# Revit family: RN 82204 Optipress-Aquaplus-Valvola diritta
name_source: partatom
category: Rohrzubehör
units: mm (PartAtom-declared; Revit-internal decimal feet)

## family parameters
Arbeitsebenenbasiert = Nein
Beim Laden mit Abzugskörper schneiden = Nein
Bemaßung runder Anschluss = Durchmesser verwenden
Gemeinsam genutzt = Nein
Immer vertikal = Ja
Teiletyp = Ventil - Zerlegung in

## types (7) — shared parameters
1.010.00.2 Number of the part of the guideline = 17
1.010.00.3 Issue date (month) of the guideline = 201601
1.010.00.4 Manufacturer name = R. Nussbaum AG
1.010.00.5 Revision date of the file = 20190528
1.100.00.3 Sort number for display sequence = 1
1.100.00.4 Product designation = Rubinetti di chiusura
1.960/3L.00.8 Link (URL) = https://www.nussbaum.ch
17.700.00.4 valve assembly type = 1
17.700.00.7 maximum operating temperature TB [°C] = 90
17.700.00.8 maximum operating pressure(working pressure) ps [1.0 · 105 Pa] = 16
Connector Visibility = Nein
EnclosingSpace Visibility = Nein

## per-type parameters (varying)
| type | 1.800.00.3 BS number | 1.810.00.3 Manufacturer’s reference number | 1.810.00.4 DATANORM number | 1.810.00.5 StLB number | 1.810.00.6 GTIN number | 17.700.00.30 product description | 17.700.00.5 nominal size DN | 17.700.00.6 kvs-value [m3/h] | CONNECTOR0_DIAMETER_dX_0r | CONNECTOR0_dX_00 | CONNECTOR0_dX_01 | CONNECTOR0_ref_dX | CONNECTOR1_DIAMETER_dX_0r | CONNECTOR1_dX_00 | CONNECTOR1_dX_01 | CONNECTOR1_ref_dX | R. Nussbaum AG 82204.22 it Visibility | R. Nussbaum AG 82204.23 it Visibility | R. Nussbaum AG 82204.24 it Visibility | R. Nussbaum AG 82204.25 it Visibility | R. Nussbaum AG 82204.26 it Visibility | R. Nussbaum AG 82204.27 it Visibility | R. Nussbaum AG 82204.28 it Visibility |
| DN 12 | 001076???0000000000000000000020070000000000000000100000000 | 82204.22 | 82204.22 | 623.422 | 7612945732965 | 82204.22, Optipress-Aquaplus-Valvola diritta, DN=12 | 12 | 2.93 | 12 mm  [stored 0.0393701 ft] | 45 mm | 23 mm | 23 mm | 12 mm  [stored 0.0393701 ft] | 23 mm | 45 mm | 23 mm | Ja | Nein | Nein | Nein | Nein | Nein | Nein |
| DN 15 | 001076???0000000000000000000020070000000000000000200000000 | 82204.23 | 82204.23 | 623.423 | 7612945732972 | 82204.23, Optipress-Aquaplus-Valvola diritta, DN=15 | 15 | 3.61 | 15 mm | 45 mm | 23 mm | 23 mm | 15 mm | 23 mm | 45 mm | 23 mm | Nein | Ja | Nein | Nein | Nein | Nein | Nein |
| DN 20 | 001076???0000000000000000000020070000000000000000300000000 | 82204.24 | 82204.24 | 623.424 | 7612945732989 | 82204.24, Optipress-Aquaplus-Valvola diritta, DN=20 | 20 | 5.86 | 20 mm | 50 mm | 27 mm | 27 mm | 20 mm | 27 mm | 50 mm | 27 mm | Nein | Nein | Ja | Nein | Nein | Nein | Nein |
| DN 25 | 001076???0000000000000000000020070000000000000000400000000 | 82204.25 | 82204.25 | 623.425 | 7612945728807 | 82204.25, Optipress-Aquaplus-Valvola diritta, DN=25 | 25 | 9.41 | 25 mm  [stored 0.082021 ft] | 58 mm | 34 mm | 34 mm | 25 mm  [stored 0.082021 ft] | 34 mm | 58 mm | 34 mm | Nein | Nein | Nein | Ja | Nein | Nein | Nein |
| DN 32 | 001076???0000000000000000000020070000000000000000500000000 | 82204.26 | 82204.26 | 623.426 | 7612945728814 | 82204.26, Optipress-Aquaplus-Valvola diritta, DN=32 | 32 | 16.13 | 32 mm | 63 mm | 37 mm | 37 mm | 32 mm | 37 mm | 63 mm | 37 mm | Nein | Nein | Nein | Nein | Ja | Nein | Nein |
| DN 40 | 001076???0000000000000000000020070000000000000000600000000 | 82204.27 | 82204.27 | 623.427 | 7612945726841 | 82204.27, Optipress-Aquaplus-Valvola diritta, DN=40 | 40 | 22.01 | 40 mm | 78 mm | 42 mm | 42 mm | 40 mm | 42 mm | 78 mm | 42 mm | Nein | Nein | Nein | Nein | Nein | Ja | Nein |
| DN 50 | 001076???0000000000000000000020070000000000000000700000000 | 82204.28 | 82204.28 | 623.428 | 7612945726858 | 82204.28, Optipress-Aquaplus-Valvola diritta, DN=50 | 50 | 35.29 | 50 mm | 88 mm | 48 mm | 48 mm | 50 mm | 48 mm | 88 mm | 48 mm | Nein | Nein | Nein | Nein | Nein | Nein | Ja |

note: [stored X ft] marks values corroborated as IEEE doubles in the binary element streams (Revit-internal decimal feet)

## geometry (parser evidence)
native form markers: Sweep x3
no freeform markers — native parametric forms only
